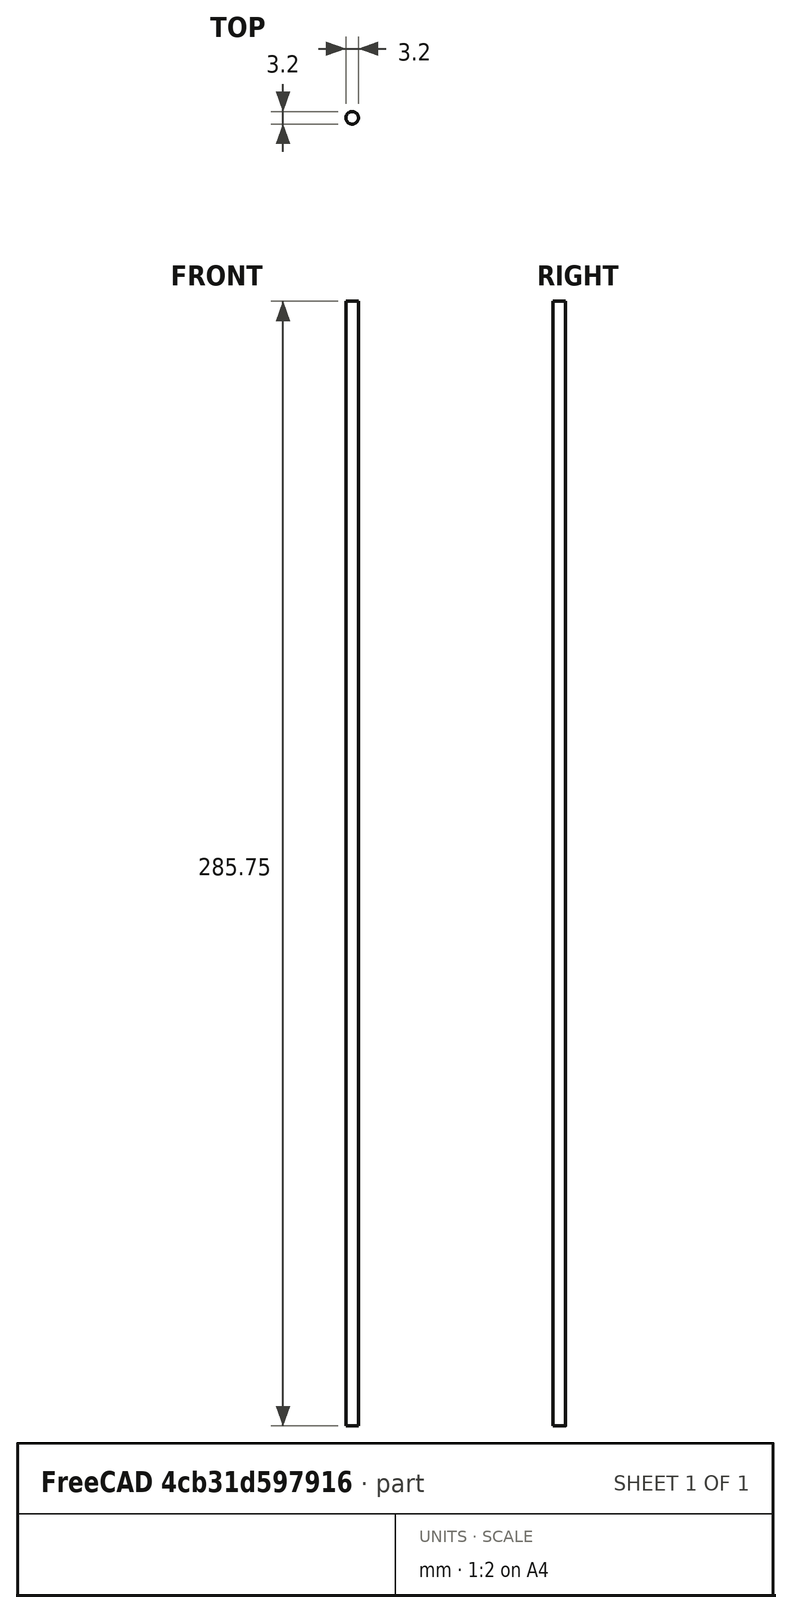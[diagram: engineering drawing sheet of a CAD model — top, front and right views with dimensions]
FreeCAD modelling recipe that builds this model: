
FCSTD DOCUMENT  (FreeCAD 0.20R29603 (Git))
Label: shelf rod
License: All rights reserved
LicenseURL: http://en.wikipedia.org/wiki/All_rights_reserved
objects: Spreadsheet::Sheet×1, Sketcher::SketchObject×1, PartDesign::Pad×1, PartDesign::Body×1
note: 4 computed .brp shape members not serialized (recipe doc carries the construction recipe); baked Part::Feature solids carry a one-line shape summary decoded from their .brp

FEATURE [Spreadsheet::Sheet] Spreadsheet  label="shelf_rod_dims"
  cells = A1=shelf_rod_diameter; B1(shelf_rod_diameter)=3.2; A2=shelf_rod_length; B2(shelf_rod_length)=285.75
FEATURE [Sketcher::SketchObject] Sketch
  FullyConstrained = true
  MapMode = 5
  Support = -> [XY_Plane]
  expr: Constraints[1] = <<shelf_rod_dims>>.shelf_rod_diameter
  sketch-geometry (1):
    g0: Circle CenterX=0 CenterY=0 CenterZ=0 NormalX=0 NormalY=0 NormalZ=1 AngleXU=0 Radius=1.6
  constraints (2):
    c: Coincident(g0,g-1)
    c: Diameter(g0) = 3.2
FEATURE [PartDesign::Pad] Pad
  Direction = (0,0,1)
  Length = 285.75
  Length2 = 10
  Profile = -> Sketch
  ReferenceAxis = -> Sketch [N_Axis]
  Type = 0
  expr: Length = <<shelf_rod_dims>>.shelf_rod_length
FEATURE [PartDesign::Body] Body  label="shelf rod"
  Group = -> [Sketch,Pad]
  Origin = -> Origin
  Tip = -> Pad
